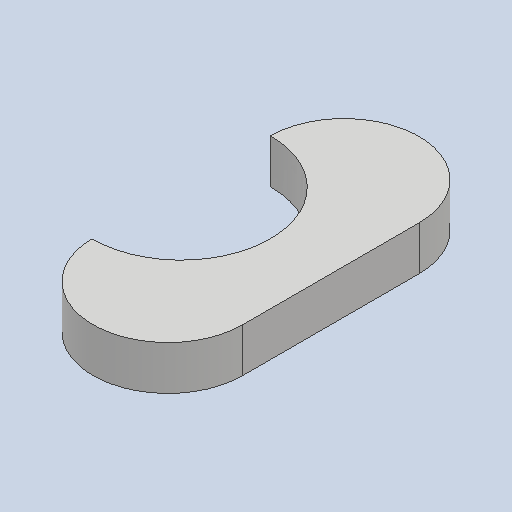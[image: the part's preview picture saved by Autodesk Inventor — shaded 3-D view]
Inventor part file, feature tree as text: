
AUTODESK INVENTOR PART (.ipt)
format: ipt  version: 2023 (Build 270158000, 158)  size: 103,936 bytes
history: native  units: mm
features: extrude x2, sketch x2
ambient origin geometry x8: Origin, YZ Plane, XZ Plane, XY Plane, X Axis, Y Axis, Z Axis, Center Point
bodies: Solid1 (feature_tree)
feature tree (4):
  extrude  "Extrusion1"  Depth=13.6mm
  extrude  "Extrusion2"  Depth=4.0mm
  sketch  "Sketch1"  dims[d0=16.0mm d1=13.6mm]
  sketch  "Sketch2"  dims[d3=4.0mm d4=0.0mm d5=16.2mm d6=0.0mm d7=0.0mm]
